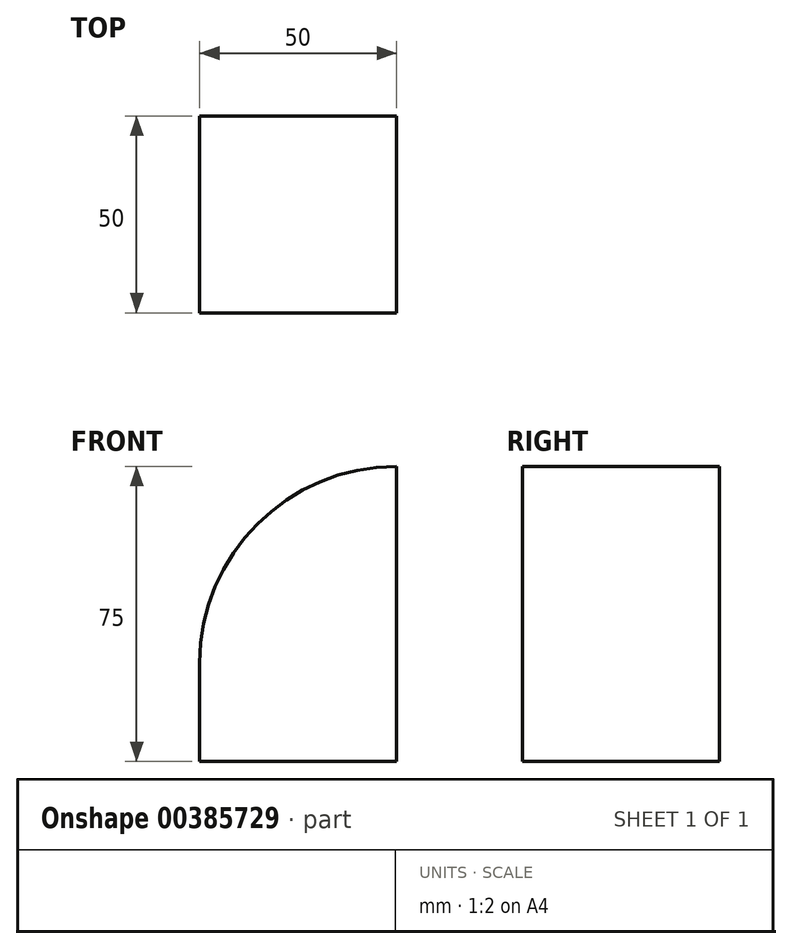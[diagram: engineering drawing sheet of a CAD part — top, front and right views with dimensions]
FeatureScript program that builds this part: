
annotation { "Feature Type Name" : "Feature", "Feature Type Description" : "" }
export const myFeature = defineFeature(function(context is Context, id is Id, definition is map)
    precondition{}
    {
        {
            var Q0;
            Q0=qCreatedBy(makeId("Top.planeOp"),FACE);
            var sketch = newSketch(context, id + "F0", { "sketchPlane" : qUnion([Q0])});
            skLineSegment(sketch, "E0.bottom", {"start": v(0, 0) * mm, "end": v(50, 0) * mm});
            skLineSegment(sketch, "E0.top", {"start": v(0, 50) * mm, "end": v(50, 50) * mm});
            skLineSegment(sketch, "E0.left", {"start": v(0, 0) * mm, "end": v(0, 50) * mm});
            skLineSegment(sketch, "E0.right", {"start": v(50, 0) * mm, "end": v(50, 50) * mm});
            skSolve(sketch);
        }
        {
            var Q0;
            Q0 = qSketchRegion(id + "F0", true);
            extrude(context, id + "F1", {"entities" : qUnion([Q0]), "depth" : 25 * mm});
        }
        {
            var Q0;
            Q0=makeQuery(id+"F1.opExtrude","CAP_FACE",FACE,{"disambiguationData":[OSD([sQuery(id+"F0.wireOp",EDGE,"E0.bottom"),sQuery(id+"F0.wireOp",EDGE,"E0.top"),sQuery(id+"F0.wireOp",EDGE,"E0.left"),sQuery(id+"F0.wireOp",EDGE,"E0.right")])],"isStart":false});
            var Q1;
            Q1=makeQuery(id+"F1.opExtrude","CAP_EDGE",EDGE,{"disambiguationData":[OSD([sQuery(id+"F0.wireOp",EDGE,"E0.right")])],"isStart":false});
            revolve(context, id + "F2", {"operationType" : NewBodyOperationType.ADD, "entities" : qUnion([Q0]), "axis" : qUnion([Q1]), "revolveType" : RevolveType.ONE_DIRECTION, "angle" : 90 * degree});
        }
    });
